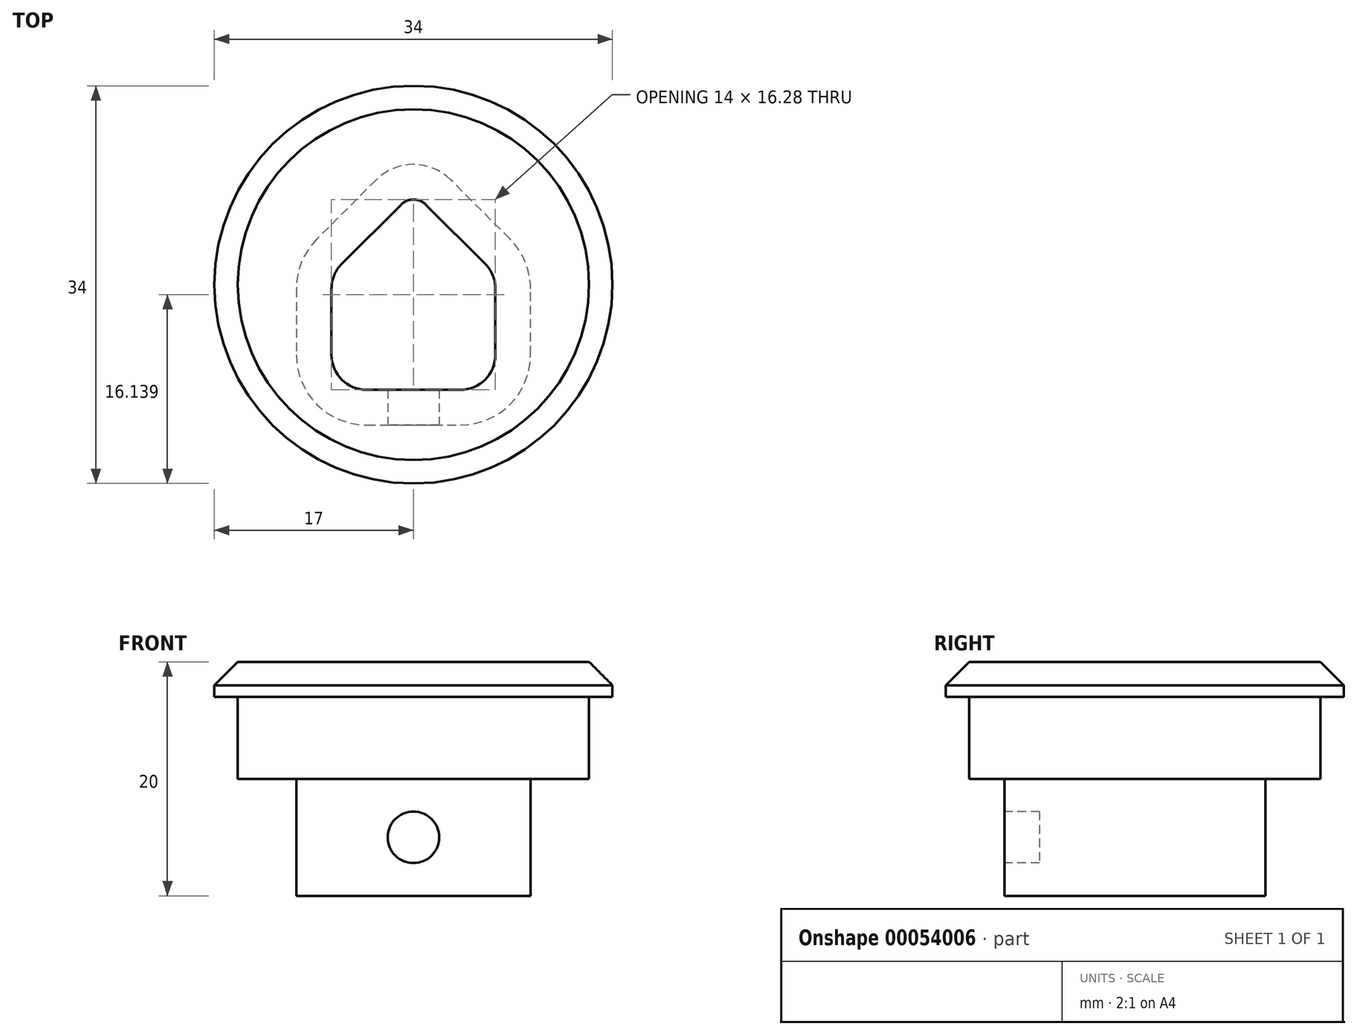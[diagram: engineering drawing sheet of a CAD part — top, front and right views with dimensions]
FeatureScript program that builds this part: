
annotation { "Feature Type Name" : "Feature", "Feature Type Description" : "" }
export const myFeature = defineFeature(function(context is Context, id is Id, definition is map)
    precondition{}
    {
        {
            var Q0;
            Q0=qCreatedBy(makeId("Right.planeOp"),FACE);
            var sketch = newSketch(context, id + "F0", { "sketchPlane" : qUnion([Q0])});
            skLineSegment(sketch, "E0", {"start": v(0, 0) * mm, "end": v(0, 10) * mm});
            skLineSegment(sketch, "E1", {"start": v(0, 10) * mm, "end": v(-15, 10) * mm});
            skLineSegment(sketch, "E2", {"start": v(-15, 10) * mm, "end": v(-17, 8) * mm});
            skLineSegment(sketch, "E3", {"start": v(-17, 8) * mm, "end": v(-17, 7) * mm});
            skLineSegment(sketch, "E4", {"start": v(-17, 7) * mm, "end": v(-15, 7) * mm});
            skLineSegment(sketch, "E5", {"start": v(-15, 7) * mm, "end": v(-15, 0) * mm});
            skLineSegment(sketch, "E6", {"start": v(-15, 0) * mm, "end": v(0, 0) * mm});
            skLineSegment(sketch, "E7", {"start": v(0, 0) * mm, "end": v(0, -4.31) * mm, "construction": true});
            skSolve(sketch);
        }
        {
            var Q0;
            Q0=makeQuery(id+"F0.imprint","IMPRINT",FACE,{"disambiguationData":[TD([[makeQuery(id+"F0.imprint","IMPRINT",EDGE,{"derivedFrom":sQuery(id+"F0.wireOp",EDGE,"E0")}),1.0]])]});
            var Q1;
            Q1=sQuery(id+"F0.wireOp",EDGE,"E7");
            revolve(context, id + "F1", {"entities" : qUnion([Q0]), "axis" : qUnion([Q1]), "revolveType" : RevolveType.FULL});
        }
        {
            var Q0;
            Q0=makeQuery(id+"F1.opRevolve","SWEPT_FACE",FACE,{"disambiguationData":[OSD([sQuery(id+"F0.wireOp",EDGE,"E1")])]});
            var sketch = newSketch(context, id + "F2", { "sketchPlane" : qUnion([Q0])});
            skLineSegment(sketch, "E8", {"start": v(-7, -6) * mm, "end": v(-7, -0.34) * mm});
            skLineSegment(sketch, "E9", {"start": v(-6.12, 1.78) * mm, "end": v(-1.06, 6.84) * mm});
            skLineSegment(sketch, "E10", {"start": v(1.06, 6.84) * mm, "end": v(6.12, 1.78) * mm});
            skLineSegment(sketch, "E11", {"start": v(7, -0.34) * mm, "end": v(7, -6) * mm});
            skLineSegment(sketch, "E12", {"start": v(4, -9) * mm, "end": v(-4, -9) * mm});
            skCircle(sketch, "E13", {"center": v(0, -2) * mm, "radius": 7 * mm, "construction": true});
            skPoint(sketch, "E14.visualSharp", {"position": v(0, 7.9) * mm});
            skArc(sketch, "E14.filletArc", {"start": v(1.06, 6.84) * mm, "mid": v(0, 7.28) * mm, "end": v(-1.06, 6.84) * mm});
            skPoint(sketch, "E15.visualSharp", {"position": v(-7, 0.9) * mm});
            skArc(sketch, "E15.filletArc", {"start": v(-6.12, 1.78) * mm, "mid": v(-6.77, 0.8) * mm, "end": v(-7, -0.34) * mm});
            skPoint(sketch, "E16.visualSharp", {"position": v(7, 0.9) * mm});
            skArc(sketch, "E16.filletArc", {"start": v(7, -0.34) * mm, "mid": v(6.77, 0.8) * mm, "end": v(6.12, 1.78) * mm});
            skPoint(sketch, "E17.visualSharp", {"position": v(7, -9) * mm});
            skArc(sketch, "E17.filletArc", {"start": v(4, -9) * mm, "mid": v(6.12, -8.12) * mm, "end": v(7, -6) * mm});
            skPoint(sketch, "E18.visualSharp", {"position": v(-7, -9) * mm});
            skArc(sketch, "E18.filletArc", {"start": v(-7, -6) * mm, "mid": v(-6.12, -8.12) * mm, "end": v(-4, -9) * mm});
            skSolve(sketch);
        }
        {
            var Q0;
            Q0=qSketchRegion(id+"F2",true);
            extrude(context, id + "F3", {"entities" : qUnion([Q0]), "operationType" : NewBodyOperationType.REMOVE, "endBound" : BoundingType.THROUGH_ALL, "oppositeDirection" : true, "depth" : 25 * mm});
        }
        {
            var Q0;
            Q0=makeQuery(id+"F1.opRevolve","SWEPT_FACE",FACE,{"disambiguationData":[OSD([sQuery(id+"F0.wireOp",EDGE,"E6")])]});
            var sketch = newSketch(context, id + "F4", { "sketchPlane" : qUnion([Q0])});
            skArc(sketch, "E19.0", {"start": v(-4, 9) * mm, "mid": v(-6.12, 8.12) * mm, "end": v(-7, 6) * mm});
            skLineSegment(sketch, "E19.1", {"start": v(-4, 9) * mm, "end": v(4, 9) * mm});
            skArc(sketch, "E19.2", {"start": v(7, 6) * mm, "mid": v(6.12, 8.12) * mm, "end": v(4, 9) * mm});
            skLineSegment(sketch, "E19.3", {"start": v(7, 6) * mm, "end": v(7, 0.34) * mm});
            skArc(sketch, "E19.4", {"start": v(6.12, -1.78) * mm, "mid": v(6.77, -0.8) * mm, "end": v(7, 0.34) * mm});
            skLineSegment(sketch, "E19.5", {"start": v(6.12, -1.78) * mm, "end": v(1.06, -6.84) * mm});
            skArc(sketch, "E19.6", {"start": v(-1.06, -6.84) * mm, "mid": v(0, -7.28) * mm, "end": v(1.06, -6.84) * mm});
            skLineSegment(sketch, "E19.8", {"start": v(-1.06, -6.84) * mm, "end": v(-6.12, -1.78) * mm});
            skLineSegment(sketch, "E20.10", {"start": v(-7, 0.34) * mm, "end": v(-7, 6) * mm});
            skArc(sketch, "E20.11", {"start": v(-7, 0.34) * mm, "mid": v(-6.77, -0.8) * mm, "end": v(-6.12, -1.78) * mm});
            skLineSegment(sketch, "E21.0", {"start": v(-4, 12) * mm, "end": v(4, 12) * mm});
            skArc(sketch, "E21.1", {"start": v(10, 6) * mm, "mid": v(8.24, 10.24) * mm, "end": v(4, 12) * mm});
            skArc(sketch, "E21.2", {"start": v(-4, 12) * mm, "mid": v(-8.24, 10.24) * mm, "end": v(-10, 6) * mm});
            skLineSegment(sketch, "E21.3", {"start": v(10, 6) * mm, "end": v(10, 0.34) * mm});
            skArc(sketch, "E21.4", {"start": v(8.24, -3.9) * mm, "mid": v(9.54, -1.95) * mm, "end": v(10, 0.34) * mm});
            skLineSegment(sketch, "E21.5", {"start": v(8.24, -3.9) * mm, "end": v(3.18, -8.96) * mm});
            skLineSegment(sketch, "E21.6", {"start": v(-10, 0.34) * mm, "end": v(-10, 6) * mm});
            skArc(sketch, "E21.7", {"start": v(-10, 0.34) * mm, "mid": v(-9.54, -1.95) * mm, "end": v(-8.24, -3.9) * mm});
            skLineSegment(sketch, "E21.8", {"start": v(-3.18, -8.96) * mm, "end": v(-8.24, -3.9) * mm});
            skArc(sketch, "E21.9", {"start": v(-3.18, -8.96) * mm, "mid": v(0, -10.28) * mm, "end": v(3.18, -8.96) * mm});
            skSolve(sketch);
        }
        {
            var Q0;
            Q0=makeQuery(id+"F4.imprint","IMPRINT",FACE,{"disambiguationData":[TD([[makeQuery(id+"F4.imprint","IMPRINT",EDGE,{"derivedFrom":sQuery(id+"F4.wireOp",EDGE,"E19.0")}),-1.0]])]});
            extrude(context, id + "F5", {"entities" : qUnion([Q0]), "operationType" : NewBodyOperationType.ADD, "depth" : 10 * mm});
        }
        {
            var Q0;
            Q0=makeQuery(id+"F5.opExtrude","SWEPT_FACE",FACE,{"disambiguationData":[OSD([sQuery(id+"F4.wireOp",EDGE,"E21.0")])]});
            var sketch = newSketch(context, id + "F6", { "sketchPlane" : qUnion([Q0])});
            skCircle(sketch, "E22", {"center": v(0, -5) * mm, "radius": 2.2 * mm});
            skSolve(sketch);
        }
        {
            var Q0;
            Q0=qSketchRegion(id+"F6",true);
            extrude(context, id + "F7", {"entities" : qUnion([Q0]), "operationType" : NewBodyOperationType.REMOVE, "endBound" : BoundingType.UP_TO_NEXT, "oppositeDirection" : true, "depth" : 25 * mm});
        }
    });
